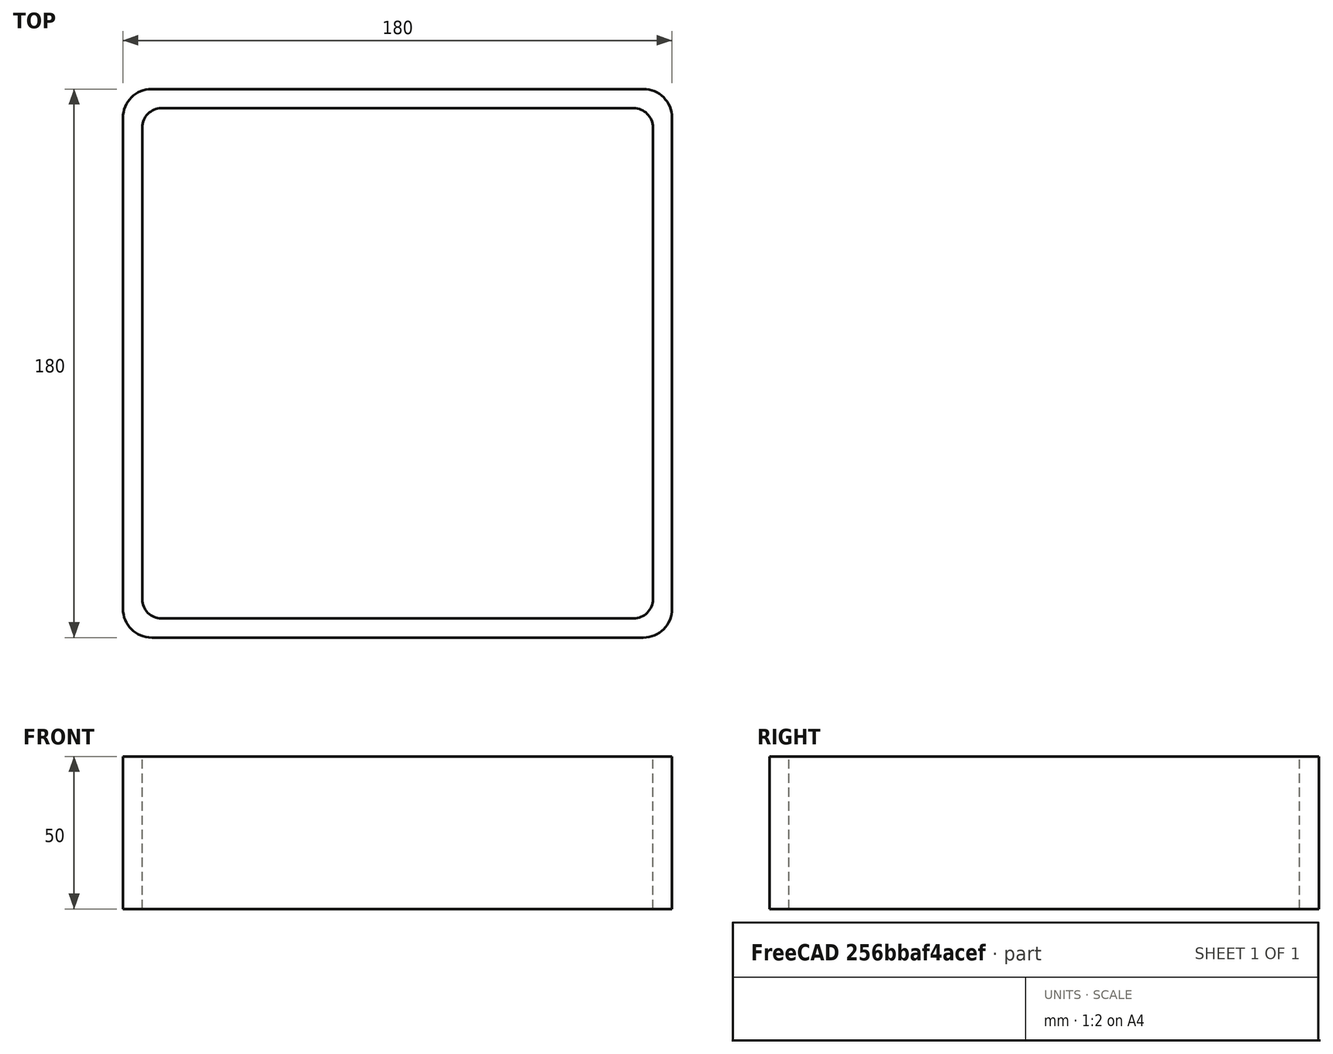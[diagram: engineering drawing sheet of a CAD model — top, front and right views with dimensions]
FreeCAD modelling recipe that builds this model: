
FCSTD DOCUMENT  (FreeCAD 0.15R4671 (Git))
Label: Square hollow section 180x180x6.3 EN10219 S235JRH
License: All rights reserved
LicenseURL: http://en.wikipedia.org/wiki/All_rights_reserved
objects: Sketcher::SketchObject×1, Part::Extrusion×1
note: 2 computed .brp shape members not serialized (recipe doc carries the construction recipe); baked Part::Feature solids carry a one-line shape summary decoded from their .brp

FEATURE [Sketcher::SketchObject] Sketch
  sketch-geometry (16):
    g0: LineSegment StartX=-77.4 StartY=83.7 StartZ=0 EndX=77.4 EndY=83.7 EndZ=0
    g1: LineSegment StartX=83.7 StartY=77.4 StartZ=0 EndX=83.7 EndY=-77.4 EndZ=0
    g2: LineSegment StartX=77.4 StartY=-83.7 StartZ=0 EndX=-77.4 EndY=-83.7 EndZ=0
    g3: LineSegment StartX=-83.7 StartY=-77.4 StartZ=0 EndX=-83.7 EndY=77.4 EndZ=0
    g4: LineSegment StartX=-80.55 StartY=90 StartZ=0 EndX=80.55 EndY=90 EndZ=0
    g5: LineSegment StartX=90 StartY=80.55 StartZ=0 EndX=90 EndY=-80.55 EndZ=0
    g6: LineSegment StartX=80.55 StartY=-90 StartZ=0 EndX=-80.55 EndY=-90 EndZ=0
    g7: LineSegment StartX=-90 StartY=-80.55 StartZ=0 EndX=-90 EndY=80.55 EndZ=0
    g8: ArcOfCircle CenterX=-77.4 CenterY=77.4 CenterZ=0 NormalX=0 NormalY=0 NormalZ=1 Radius=6.3 StartAngle=1.5708 EndAngle=3.14159
    g9: ArcOfCircle CenterX=77.4 CenterY=77.4 CenterZ=0 NormalX=0 NormalY=0 NormalZ=1 Radius=6.3 StartAngle=0 EndAngle=1.5708
    g10: ArcOfCircle CenterX=77.4 CenterY=-77.4 CenterZ=0 NormalX=0 NormalY=0 NormalZ=1 Radius=6.3 StartAngle=4.71239 EndAngle=6.28319
    g11: ArcOfCircle CenterX=-77.4 CenterY=-77.4 CenterZ=0 NormalX=0 NormalY=0 NormalZ=1 Radius=6.3 StartAngle=3.14159 EndAngle=4.71239
    g12: ArcOfCircle CenterX=80.55 CenterY=80.55 CenterZ=0 NormalX=0 NormalY=0 NormalZ=1 Radius=9.45 StartAngle=0 EndAngle=1.5708
    g13: ArcOfCircle CenterX=80.55 CenterY=-80.55 CenterZ=0 NormalX=0 NormalY=0 NormalZ=1 Radius=9.45 StartAngle=4.71239 EndAngle=6.28319
    g14: ArcOfCircle CenterX=-80.55 CenterY=-80.55 CenterZ=0 NormalX=0 NormalY=0 NormalZ=1 Radius=9.45 StartAngle=3.14159 EndAngle=4.71239
    g15: ArcOfCircle CenterX=-80.55 CenterY=80.55 CenterZ=0 NormalX=0 NormalY=0 NormalZ=1 Radius=9.45 StartAngle=1.5708 EndAngle=3.14159
  constraints (36):
    c: Horizontal(g2)
    c: Vertical(g3)
    c: Horizontal(g6)
    c: Vertical(g7)
    c: Tangent(g3,g8) = 1.5708
    c: Tangent(g0,g8) = 1.5708
    c: Tangent(g0,g9) = 1.5708
    c: Tangent(g1,g9) = 1.5708
    c: Tangent(g1,g10) = 1.5708
    c: Tangent(g2,g10) = 1.5708
    c: Tangent(g2,g11) = 1.5708
    c: Tangent(g3,g11) = 1.5708
    c: Tangent(g4,g12) = 1.5708
    c: Tangent(g5,g12) = 1.5708
    c: Tangent(g5,g13) = 1.5708
    c: Tangent(g6,g13) = 1.5708
    c: Tangent(g6,g14) = 1.5708
    c: Tangent(g7,g14) = 1.5708
    c: Tangent(g7,g15) = 1.5708
    c: Tangent(g4,g15) = 1.5708
    c: Equal(g9,g8)
    c: Equal(g9,g11)
    c: Equal(g9,g10)
    c: Equal(g12,g15)
    c: Equal(g12,g14)
    c: Equal(g12,g13)
    c: Symmetric(g4,g6,g-1)
    c: Symmetric(g7,g5,g-2)
    c: DistanceY(g4,g6) = -180
    c: DistanceX(g7,g5) = 180
    c: Symmetric(g3,g1,g-2)
    c: Symmetric(g0,g2,g-1)
    c: DistanceY(g0,g4) = 6.3
    c: DistanceX(g5,g1) = -6.3
    c: Radius(g9) = 6.3
    c: Radius(g12) = 9.45
FEATURE [Part::Extrusion] Extrude  label="Square hollow section 180x180x6.3 EN10219 S235JRH"
  Base = -> Sketch
  Dir = (0,0,50)
  Solid = true
